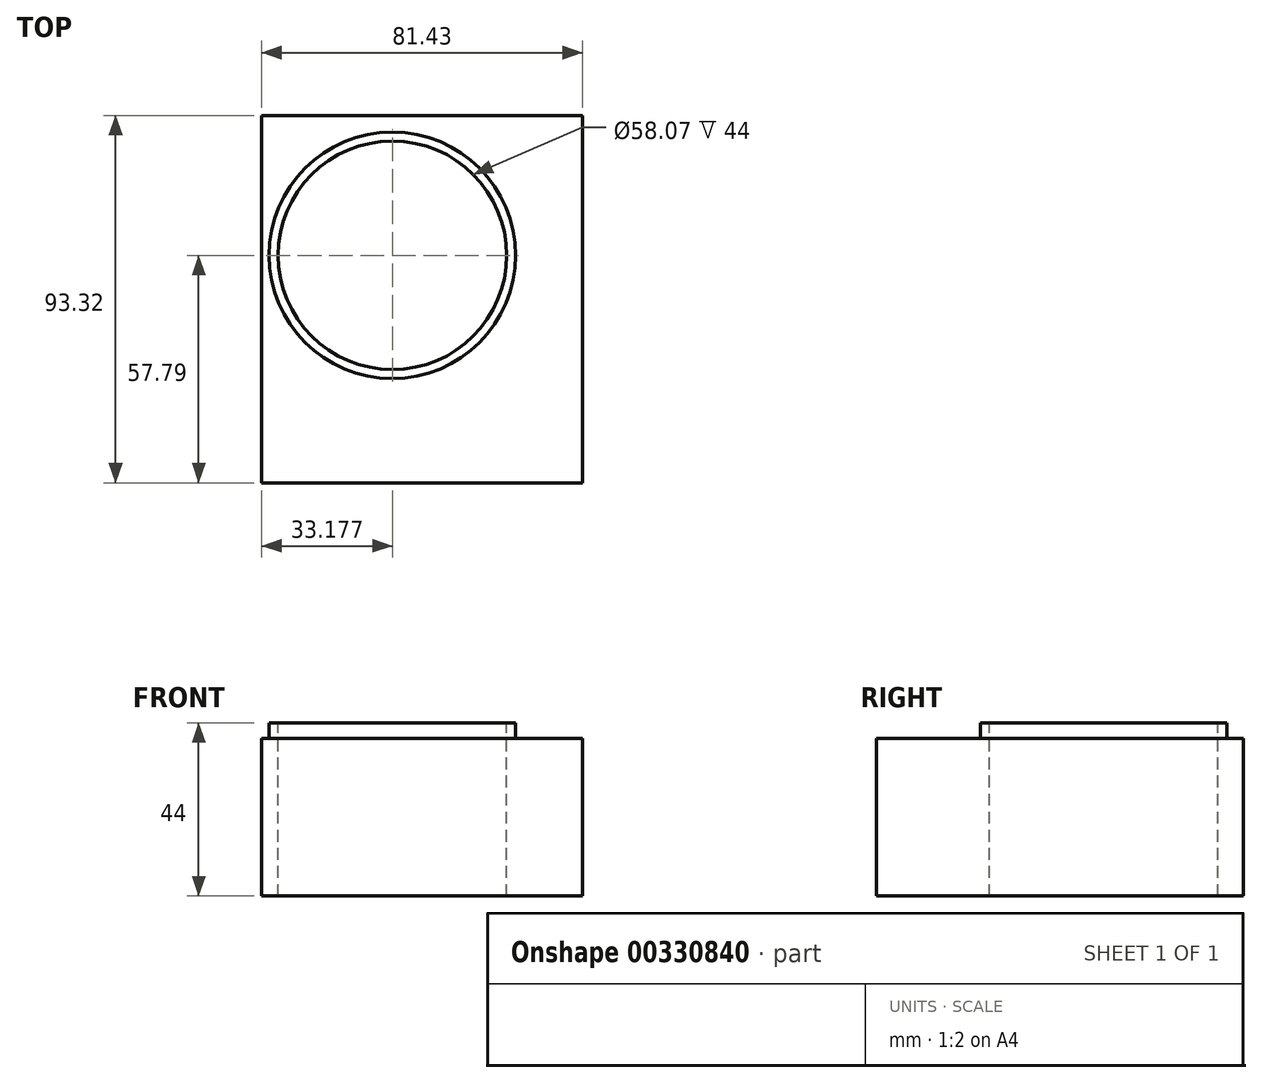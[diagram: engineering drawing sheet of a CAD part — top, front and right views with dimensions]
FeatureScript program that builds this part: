
annotation { "Feature Type Name" : "Feature", "Feature Type Description" : "" }
export const myFeature = defineFeature(function(context is Context, id is Id, definition is map)
    precondition{}
    {
        {
            var Q0;
            Q0=qCreatedBy(makeId("Top.planeOp"),FACE);
            var sketch = newSketch(context, id + "F0", { "sketchPlane" : qUnion([Q0])});
            skLineSegment(sketch, "E0.bottom", {"start": v(-69.9, 35.53) * mm, "end": v(11.54, 35.53) * mm});
            skLineSegment(sketch, "E0.top", {"start": v(-69.9, -57.8) * mm, "end": v(11.54, -57.8) * mm});
            skLineSegment(sketch, "E0.left", {"start": v(-69.9, 35.53) * mm, "end": v(-69.9, -57.8) * mm});
            skLineSegment(sketch, "E0.right", {"start": v(11.54, 35.53) * mm, "end": v(11.54, -57.8) * mm});
            skSolve(sketch);
        }
        {
            var Q0;
            Q0=makeQuery(id+"F0.imprint","IMPRINT",FACE,{"disambiguationData":[TD([[makeQuery(id+"F0.imprint","IMPRINT",EDGE,{"derivedFrom":sQuery(id+"F0.wireOp",EDGE,"E0.bottom")}),-1.0]])]});
            extrude(context, id + "F1", {"entities" : qUnion([Q0]), "depth" : 40 * mm});
        }
        {
            var Q0;
            Q0=makeQuery(id+"F1.opExtrude","CAP_FACE",FACE,{"disambiguationData":[OSD([sQuery(id+"F0.wireOp",EDGE,"E0.bottom"),sQuery(id+"F0.wireOp",EDGE,"E0.top"),sQuery(id+"F0.wireOp",EDGE,"E0.left"),sQuery(id+"F0.wireOp",EDGE,"E0.right")])],"isStart":false});
            var sketch = newSketch(context, id + "F2", { "sketchPlane" : qUnion([Q0])});
            skCircle(sketch, "E1", {"center": v(-36.71, 0) * mm, "radius": 29.03 * mm});
            skSolve(sketch);
        }
        {
            var Q0;
            Q0=makeQuery(id+"F2.imprint","IMPRINT",FACE,{"disambiguationData":[TD([[makeQuery(id+"F2.imprint","IMPRINT",EDGE,{"derivedFrom":sQuery(id+"F2.wireOp",EDGE,"E1")}),1.0]])]});
            extrude(context, id + "F3", {"entities" : qUnion([Q0]), "operationType" : NewBodyOperationType.REMOVE, "oppositeDirection" : true, "depth" : 50 * mm});
        }
        {
            var Q0;
            Q0=makeQuery(id+"F1.opExtrude","CAP_FACE",FACE,{"disambiguationData":[OSD([sQuery(id+"F0.wireOp",EDGE,"E0.bottom"),sQuery(id+"F0.wireOp",EDGE,"E0.top"),sQuery(id+"F0.wireOp",EDGE,"E0.left"),sQuery(id+"F0.wireOp",EDGE,"E0.right")])],"isStart":false});
            var sketch = newSketch(context, id + "F4", { "sketchPlane" : qUnion([Q0])});
            skCircle(sketch, "E2", {"center": v(-36.71, 0) * mm, "radius": 31.3 * mm});
            skSolve(sketch);
        }
        {
            var Q0;
            Q0=makeQuery(id+"F4.imprint","IMPRINT",FACE,{"disambiguationData":[TD([[makeQuery(id+"F4.imprint","IMPRINT",EDGE,{"derivedFrom":sQuery(id+"F4.wireOp",EDGE,"E2")}),1.0]])]});
            extrude(context, id + "F5", {"entities" : qUnion([Q0]), "operationType" : NewBodyOperationType.ADD, "depth" : 4 * mm});
        }
    });
